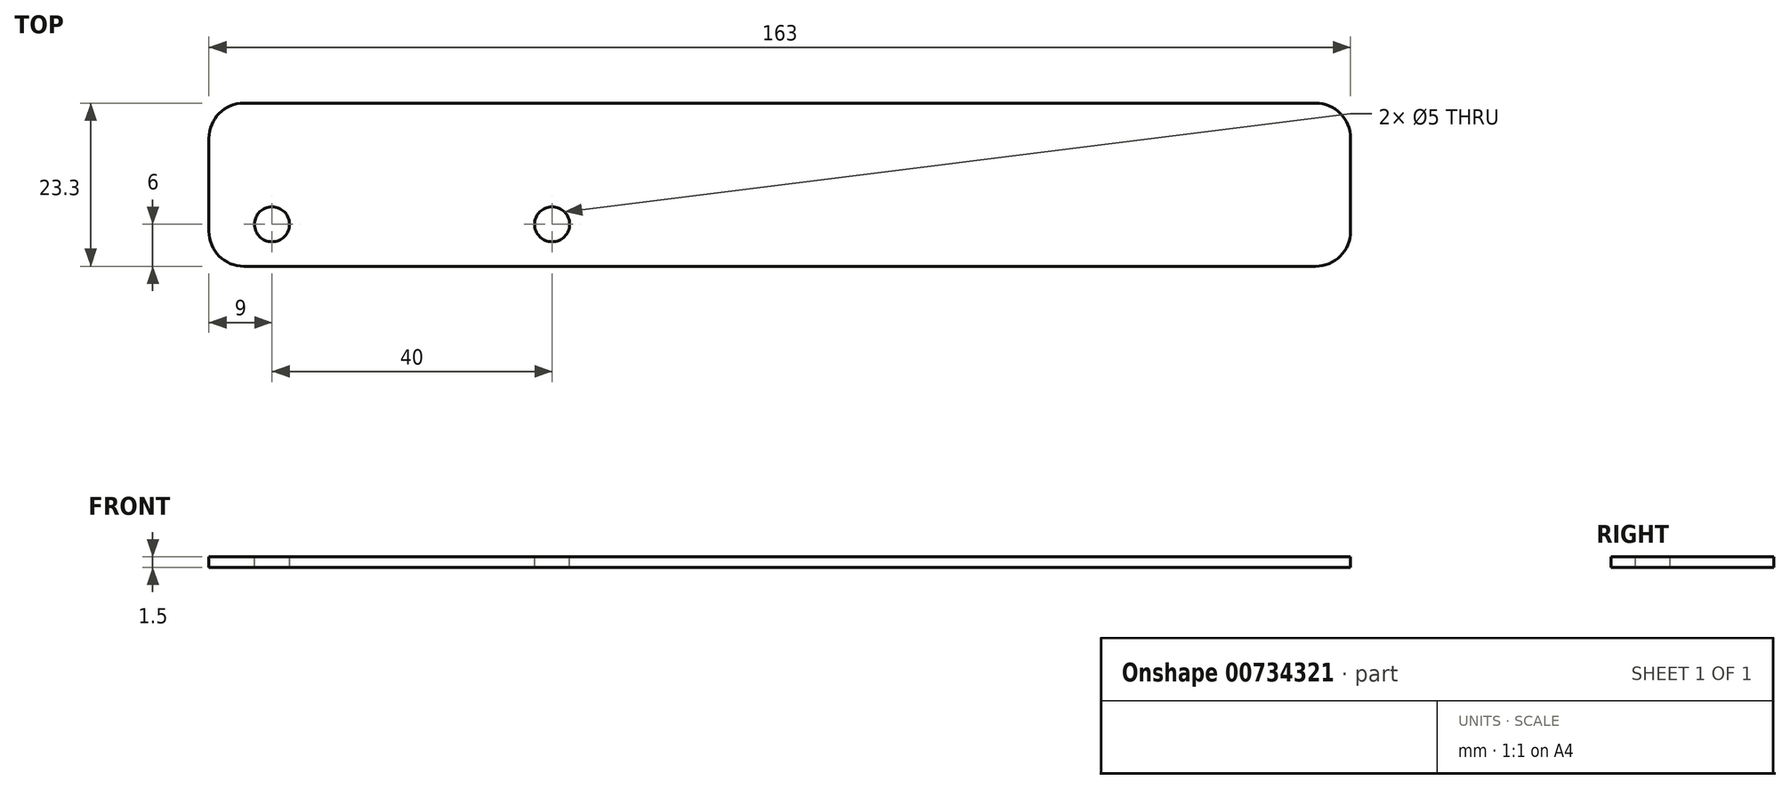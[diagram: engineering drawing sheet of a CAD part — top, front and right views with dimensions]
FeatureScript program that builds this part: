
annotation { "Feature Type Name" : "Feature", "Feature Type Description" : "" }
export const myFeature = defineFeature(function(context is Context, id is Id, definition is map)
    precondition{}
    {
        {
            var Q0;
            Q0=qCreatedBy(makeId("Top.planeOp"),FACE);
            var sketch = newSketch(context, id + "F0", { "sketchPlane" : qUnion([Q0])});
            skLineSegment(sketch, "E0.bottom", {"start": v(81.5, -11.65) * mm, "end": v(-81.5, -11.65) * mm});
            skLineSegment(sketch, "E0.top", {"start": v(81.5, 11.65) * mm, "end": v(-81.5, 11.65) * mm});
            skLineSegment(sketch, "E0.left", {"start": v(81.5, -11.65) * mm, "end": v(81.5, 11.65) * mm});
            skLineSegment(sketch, "E0.right", {"start": v(-81.5, -11.65) * mm, "end": v(-81.5, 11.65) * mm});
            skPoint(sketch, "E0.middle", {"position": v(0, 0) * mm});
            skSolve(sketch);
        }
        {
            var Q0;
            Q0 = qSketchRegion(id + "F0", true);
            extrude(context, id + "F1", {"entities" : qUnion([Q0]), "depth" : 1.5 * mm, "offsetDistance" : 25.4 * mm});
        }
        {
            var Q0;
            Q0=makeQuery(id+"F1.opExtrude","CAP_FACE",FACE,{"disambiguationData":[OSD([sQuery(id+"F0.wireOp",EDGE,"E0.bottom"),sQuery(id+"F0.wireOp",EDGE,"E0.top"),sQuery(id+"F0.wireOp",EDGE,"E0.left"),sQuery(id+"F0.wireOp",EDGE,"E0.right")])],"isStart":false});
            var sketch = newSketch(context, id + "F2", { "sketchPlane" : qUnion([Q0])});
            skLineSegment(sketch, "E1", {"start": v(-81.5, -5.65) * mm, "end": v(81.5, -5.65) * mm, "construction": true});
            skCircle(sketch, "E2", {"center": v(-72.5, -5.65) * mm, "radius": 2.5 * mm});
            skCircle(sketch, "E3", {"center": v(-32.5, -5.65) * mm, "radius": 2.5 * mm});
            skSolve(sketch);
        }
        {
            var Q0;
            Q0=makeQuery(id+"F2.imprint","IMPRINT",FACE,{"disambiguationData":[TD([[makeQuery(id+"F2.imprint","IMPRINT",EDGE,{"derivedFrom":sQuery(id+"F2.wireOp",EDGE,"E2")}),1.0]])]});
            var Q1;
            Q1=makeQuery(id+"F2.imprint","IMPRINT",FACE,{"disambiguationData":[TD([[makeQuery(id+"F2.imprint","IMPRINT",EDGE,{"derivedFrom":sQuery(id+"F2.wireOp",EDGE,"E3")}),1.0]])]});
            extrude(context, id + "F3", {"entities" : qUnion([Q0, Q1]), "operationType" : NewBodyOperationType.REMOVE, "endBound" : BoundingType.THROUGH_ALL, "oppositeDirection" : true, "depth" : 25 * mm, "offsetDistance" : 25 * mm});
        }
        {
            var Q0;
            Q0=makeQuery(id+"F1.opExtrude","SWEPT_EDGE",EDGE,{"disambiguationData":[OSD([sQuery(id+"F0.wireOp",EDGE,"E0.top"),sQuery(id+"F0.wireOp",EDGE,"E0.right")])]});
            var Q1;
            Q1=makeQuery(id+"F1.opExtrude","SWEPT_EDGE",EDGE,{"disambiguationData":[OSD([sQuery(id+"F0.wireOp",EDGE,"E0.bottom"),sQuery(id+"F0.wireOp",EDGE,"E0.right")])]});
            var Q2;
            Q2=makeQuery(id+"F1.opExtrude","SWEPT_EDGE",EDGE,{"disambiguationData":[OSD([sQuery(id+"F0.wireOp",EDGE,"E0.bottom"),sQuery(id+"F0.wireOp",EDGE,"E0.left")])]});
            var Q3;
            Q3=makeQuery(id+"F1.opExtrude","SWEPT_EDGE",EDGE,{"disambiguationData":[OSD([sQuery(id+"F0.wireOp",EDGE,"E0.top"),sQuery(id+"F0.wireOp",EDGE,"E0.left")])]});
            fillet(context, id + "F4", {"entities" : qUnion([Q0, Q1, Q2, Q3]), "radius" : 5 * mm, "tangentPropagation" : true, "allowEdgeOverflow" : false});
        }
    });
